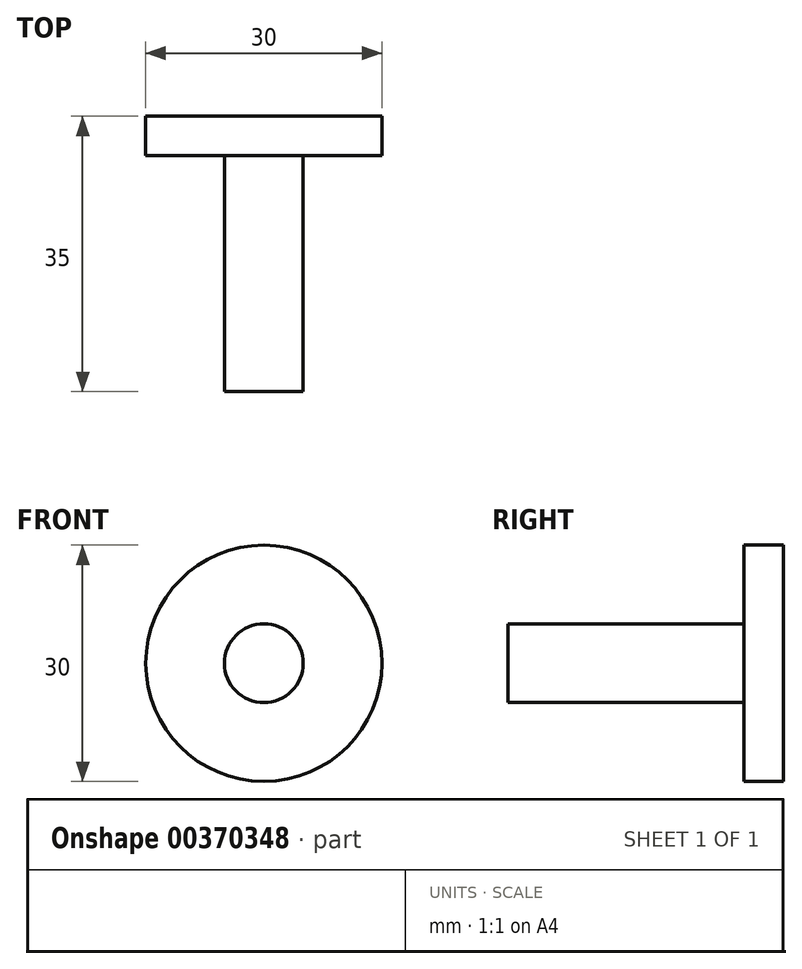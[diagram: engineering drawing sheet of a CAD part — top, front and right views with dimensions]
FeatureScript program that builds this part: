
annotation { "Feature Type Name" : "Feature", "Feature Type Description" : "" }
export const myFeature = defineFeature(function(context is Context, id is Id, definition is map)
    precondition{}
    {
        {
            var Q0;
            Q0=qCreatedBy(makeId("Right.planeOp"),FACE);
            var sketch = newSketch(context, id + "F0", { "sketchPlane" : qUnion([Q0])});
            skLineSegment(sketch, "E0", {"start": v(0, 0) * mm, "end": v(-30, 0) * mm});
            skLineSegment(sketch, "E1", {"start": v(-30, 0) * mm, "end": v(-30, 5) * mm});
            skLineSegment(sketch, "E2", {"start": v(-30, 5) * mm, "end": v(0, 5) * mm});
            skLineSegment(sketch, "E3", {"start": v(0, 5) * mm, "end": v(0, 15) * mm});
            skLineSegment(sketch, "E4", {"start": v(0, 15) * mm, "end": v(5, 15) * mm});
            skLineSegment(sketch, "E5", {"start": v(5, 15) * mm, "end": v(5, 0) * mm});
            skLineSegment(sketch, "E6", {"start": v(5, 0) * mm, "end": v(0, 0) * mm});
            skSolve(sketch);
        }
        {
            var Q0;
            Q0=makeQuery(id+"F0.imprint","IMPRINT",FACE,{"disambiguationData":[TD([[makeQuery(id+"F0.imprint","IMPRINT",EDGE,{"derivedFrom":sQuery(id+"F0.wireOp",EDGE,"E0")}),-1.0]])]});
            var Q1;
            Q1=sQuery(id+"F0.wireOp",EDGE,"E0");
            revolve(context, id + "F1", {"entities" : qUnion([Q0]), "axis" : qUnion([Q1]), "revolveType" : RevolveType.FULL});
        }
    });
